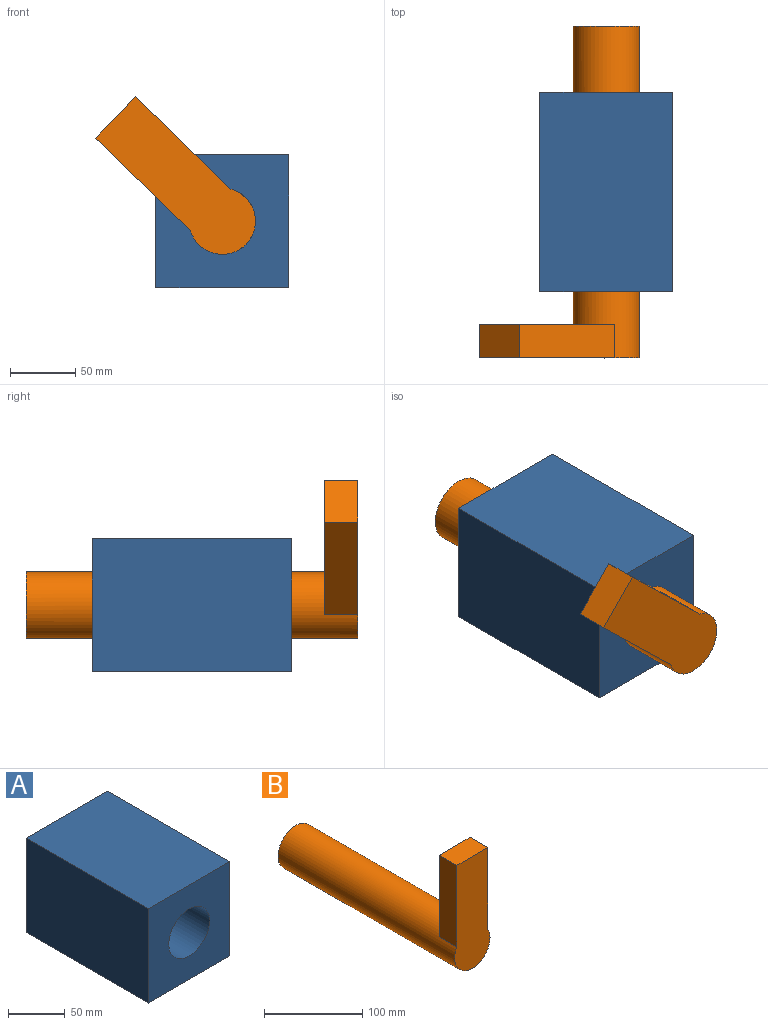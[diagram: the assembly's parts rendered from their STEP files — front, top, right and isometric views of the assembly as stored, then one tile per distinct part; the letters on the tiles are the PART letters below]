
ASSEMBLY  parts=2 mates=1
PART A: 7 faces, bbox 101.6x152.4x101.6 mm
  f0: plane 152.4x101.6mm, normal (0,0,1), area 15483.8mm2, adj f1,f4,f5,f6
  f1: plane 152.4x101.6mm, normal (-1,0,0), area 15483.8mm2, adj f0,f2,f5,f6
  f2: plane 152.4x101.6mm, normal (0,0,-1), area 15483.8mm2, adj f1,f4,f5,f6
  f3: cylinder r=25.4mm len=152.4mm, axis (0,1,0), area 24322mm2, adj f5,f6
  f4: plane 152.4x101.6mm, normal (1,0,0), area 15483.8mm2, adj f0,f2,f5,f6
  f5: plane 101.6x101.6mm, normal (0,-1,0), area 8295.7mm2, adj f0,f1,f2,f3,f4
  f6: plane 101.6x101.6mm, normal (0,1,0), area 8295.7mm2, adj f0,f1,f2,f3,f4
PART B: 7 faces, bbox 50.8x254x139.3 mm
  f0: cylinder r=25.4mm len=254mm, axis (0,1,0), area 39162.7mm2, adj f1,f2,f3,f4,f5
  f1: plane 139.31x50.8mm, normal (0,-1,0), area 6127.9mm2, adj f0,f3,f5,f6
  f2: plane 50.8x50.8mm, normal (0,1,0), area 2026.8mm2, adj f0
  f3: plane 101.6x25.4mm, normal (1,0,0), area 2580.6mm2, adj f0,f1,f4,f6
  f4: plane 101.6x44.43mm, normal (0,1,0), area 4101.1mm2, adj f0,f3,f5,f6
  f5: plane 101.6x25.4mm, normal (-1,0,0), area 2580.6mm2, adj f0,f1,f4,f6
  f6: plane 44.43x25.4mm, normal (0,0,1), area 1128.6mm2, adj f1,f3,f4,f5
PLACE A rot(axis=(0,1,0),90deg) t=(0,0,-50.8)mm
PLACE B rot(axis=(0,-1,0),45.7deg) t=(0,0,-50.8)mm
MATE revolute B.f0 <-> A.f3  axis (0,1,0) through (0,0,-50.8)mm
